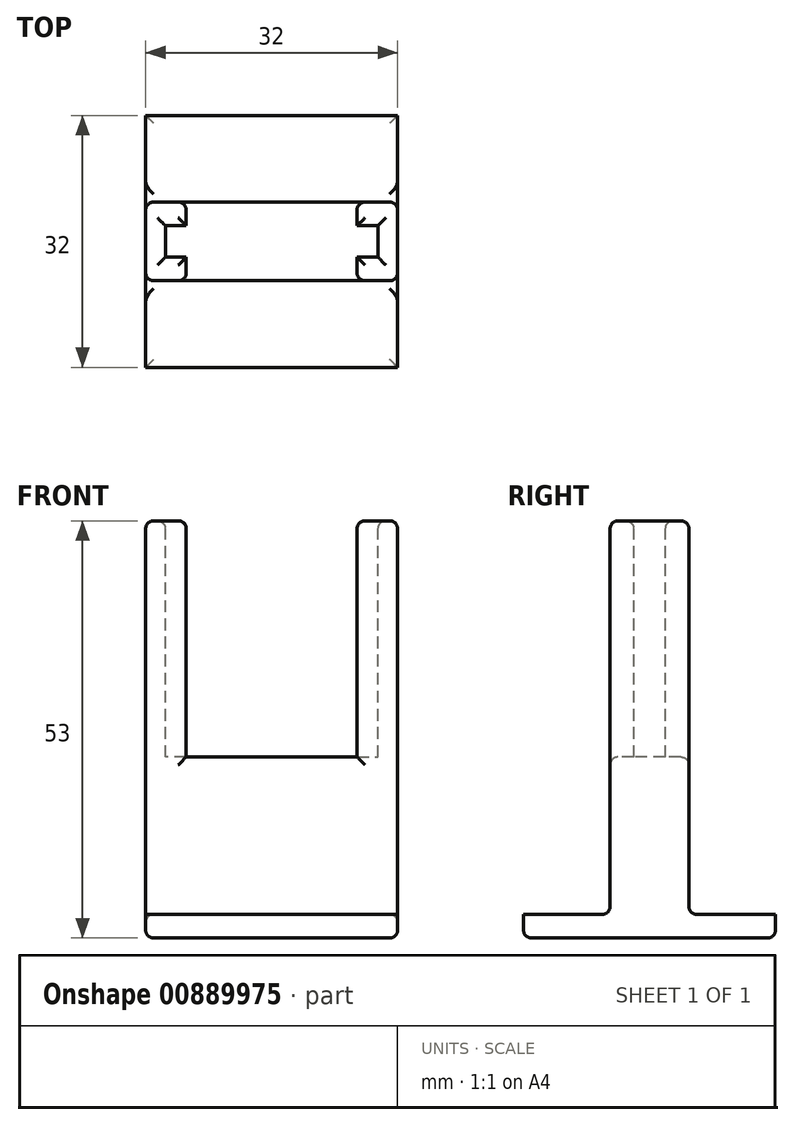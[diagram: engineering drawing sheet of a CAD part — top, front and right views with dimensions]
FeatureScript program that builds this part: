
annotation { "Feature Type Name" : "Feature", "Feature Type Description" : "" }
export const myFeature = defineFeature(function(context is Context, id is Id, definition is map)
    precondition{}
    {
        {
            var Q0;
            Q0=qCreatedBy(makeId("Top.planeOp"),FACE);
            var sketch = newSketch(context, id + "F0", { "sketchPlane" : qUnion([Q0])});
            skLineSegment(sketch, "E0.bottom", {"start": v(-16, 16) * mm, "end": v(16, 16) * mm});
            skLineSegment(sketch, "E0.top", {"start": v(-16, -16) * mm, "end": v(16, -16) * mm});
            skLineSegment(sketch, "E0.left", {"start": v(-16, 16) * mm, "end": v(-16, -16) * mm});
            skLineSegment(sketch, "E0.right", {"start": v(16, 16) * mm, "end": v(16, -16) * mm});
            skSolve(sketch);
        }
        {
            var Q0;
            Q0 = qSketchRegion(id + "F0", true);
            extrude(context, id + "F1", {"entities" : qUnion([Q0]), "depth" : 3 * mm, "offsetDistance" : 25 * mm});
        }
        {
            var Q0;
            Q0=makeQuery(id+"F1.opExtrude","CAP_FACE",FACE,{"disambiguationData":[OSD([sQuery(id+"F0.wireOp",EDGE,"E0.bottom"),sQuery(id+"F0.wireOp",EDGE,"E0.top"),sQuery(id+"F0.wireOp",EDGE,"E0.left"),sQuery(id+"F0.wireOp",EDGE,"E0.right")])],"isStart":false});
            var sketch = newSketch(context, id + "F2", { "sketchPlane" : qUnion([Q0])});
            skLineSegment(sketch, "E1.bottom", {"start": v(-16, 5) * mm, "end": v(16, 5) * mm});
            skLineSegment(sketch, "E1.top", {"start": v(-16, -5) * mm, "end": v(16, -5) * mm});
            skLineSegment(sketch, "E1.left", {"start": v(-16, 5) * mm, "end": v(-16, -5) * mm});
            skLineSegment(sketch, "E1.right", {"start": v(16, 5) * mm, "end": v(16, -5) * mm});
            skSolve(sketch);
        }
        {
            var Q0;
            Q0 = qSketchRegion(id + "F2", true);
            extrude(context, id + "F3", {"entities" : qUnion([Q0]), "operationType" : NewBodyOperationType.ADD, "depth" : 50 * mm, "offsetDistance" : 25 * mm});
        }
        {
            var Q0;
            Q0=makeQuery(id+"F3.opExtrude","CAP_FACE",FACE,{"disambiguationData":[OSD([sQuery(id+"F2.wireOp",EDGE,"E1.bottom"),sQuery(id+"F2.wireOp",EDGE,"E1.top"),sQuery(id+"F2.wireOp",EDGE,"E1.left"),sQuery(id+"F2.wireOp",EDGE,"E1.right")])],"isStart":false});
            var sketch = newSketch(context, id + "F4", { "sketchPlane" : qUnion([Q0])});
            skLineSegment(sketch, "E2", {"start": v(-10.86, 5) * mm, "end": v(-10.86, 2) * mm});
            skLineSegment(sketch, "E3", {"start": v(-10.86, 2) * mm, "end": v(-13.5, 2) * mm});
            skLineSegment(sketch, "E4", {"start": v(-13.5, 2) * mm, "end": v(-13.5, -2) * mm});
            skLineSegment(sketch, "E5", {"start": v(-13.5, -2) * mm, "end": v(-10.86, -2) * mm});
            skLineSegment(sketch, "E6", {"start": v(-10.86, -2) * mm, "end": v(-10.86, -5) * mm});
            skLineSegment(sketch, "E7", {"start": v(-10.86, -5) * mm, "end": v(10.86, -5) * mm});
            skLineSegment(sketch, "E8", {"start": v(10.86, -5) * mm, "end": v(10.86, -2) * mm});
            skLineSegment(sketch, "E9", {"start": v(10.86, -2) * mm, "end": v(13.5, -2) * mm});
            skLineSegment(sketch, "E10", {"start": v(13.5, -2) * mm, "end": v(13.5, 2) * mm});
            skLineSegment(sketch, "E11", {"start": v(13.5, 2) * mm, "end": v(10.86, 2) * mm});
            skLineSegment(sketch, "E12", {"start": v(10.86, 2) * mm, "end": v(10.86, 5) * mm});
            skLineSegment(sketch, "E13", {"start": v(10.86, 5) * mm, "end": v(-10.86, 5) * mm});
            skSolve(sketch);
        }
        {
            var Q0;
            Q0 = qSketchRegion(id + "F4", true);
            extrude(context, id + "F5", {"entities" : qUnion([Q0]), "operationType" : NewBodyOperationType.REMOVE, "oppositeDirection" : true, "depth" : 30 * mm, "offsetDistance" : 25 * mm});
        }
        {
            var Q0;
            Q0=makeQuery(id+"F1.opExtrude","CAP_FACE",FACE,{"disambiguationData":[OSD([sQuery(id+"F0.wireOp",EDGE,"E0.bottom"),sQuery(id+"F0.wireOp",EDGE,"E0.top"),sQuery(id+"F0.wireOp",EDGE,"E0.left"),sQuery(id+"F0.wireOp",EDGE,"E0.right")])],"isStart":true});
            var Q1;
            Q1=makeQuery(id+"F3.opExtrude","SWEPT_FACE",FACE,{"disambiguationData":[OSD([sQuery(id+"F2.wireOp",EDGE,"E1.top")])]});
            var Q2;
            Q2=makeQuery(id+"F3.opExtrude","SWEPT_FACE",FACE,{"disambiguationData":[OSD([sQuery(id+"F2.wireOp",EDGE,"E1.bottom")])]});
            var Q3;
            {var subQ0=sQuery(id+"F2.wireOp",EDGE,"E1.top");var subQ1=sQuery(id+"F2.wireOp",EDGE,"E1.right");var subQ2=sQuery(id+"F2.wireOp",EDGE,"E1.bottom");Q3=makeQuery(id+"F5.boolean.opBoolean","SPLIT",FACE,{"disambiguationData":[TD([makeQuery(id+"F1.opExtrude","SWEPT_FACE",FACE,{"disambiguationData":[OSD([sQuery(id+"F0.wireOp",EDGE,"E0.right")])]})])],"derivedFrom":makeQuery(id+"F3.opExtrude","CAP_FACE",FACE,{"disambiguationData":[OSD([subQ2,subQ0,sQuery(id+"F2.wireOp",EDGE,"E1.left"),subQ1])],"isStart":false})});}
            var Q4;
            {var subQ0=sQuery(id+"F2.wireOp",EDGE,"E1.left");var subQ1=sQuery(id+"F2.wireOp",EDGE,"E1.top");var subQ2=sQuery(id+"F2.wireOp",EDGE,"E1.bottom");Q4=makeQuery(id+"F5.boolean.opBoolean","SPLIT",FACE,{"disambiguationData":[TD([makeQuery(id+"F1.opExtrude","SWEPT_FACE",FACE,{"disambiguationData":[OSD([sQuery(id+"F0.wireOp",EDGE,"E0.left")])]})])],"derivedFrom":makeQuery(id+"F3.opExtrude","CAP_FACE",FACE,{"disambiguationData":[OSD([subQ2,subQ1,subQ0,sQuery(id+"F2.wireOp",EDGE,"E1.right")])],"isStart":false})});}
            fillet(context, id + "F6", {"entities" : qUnion([Q0, Q1, Q2, Q3, Q4]), "radius" : 1 * mm, "tangentPropagation" : true, "allowEdgeOverflow" : false});
        }
    });
